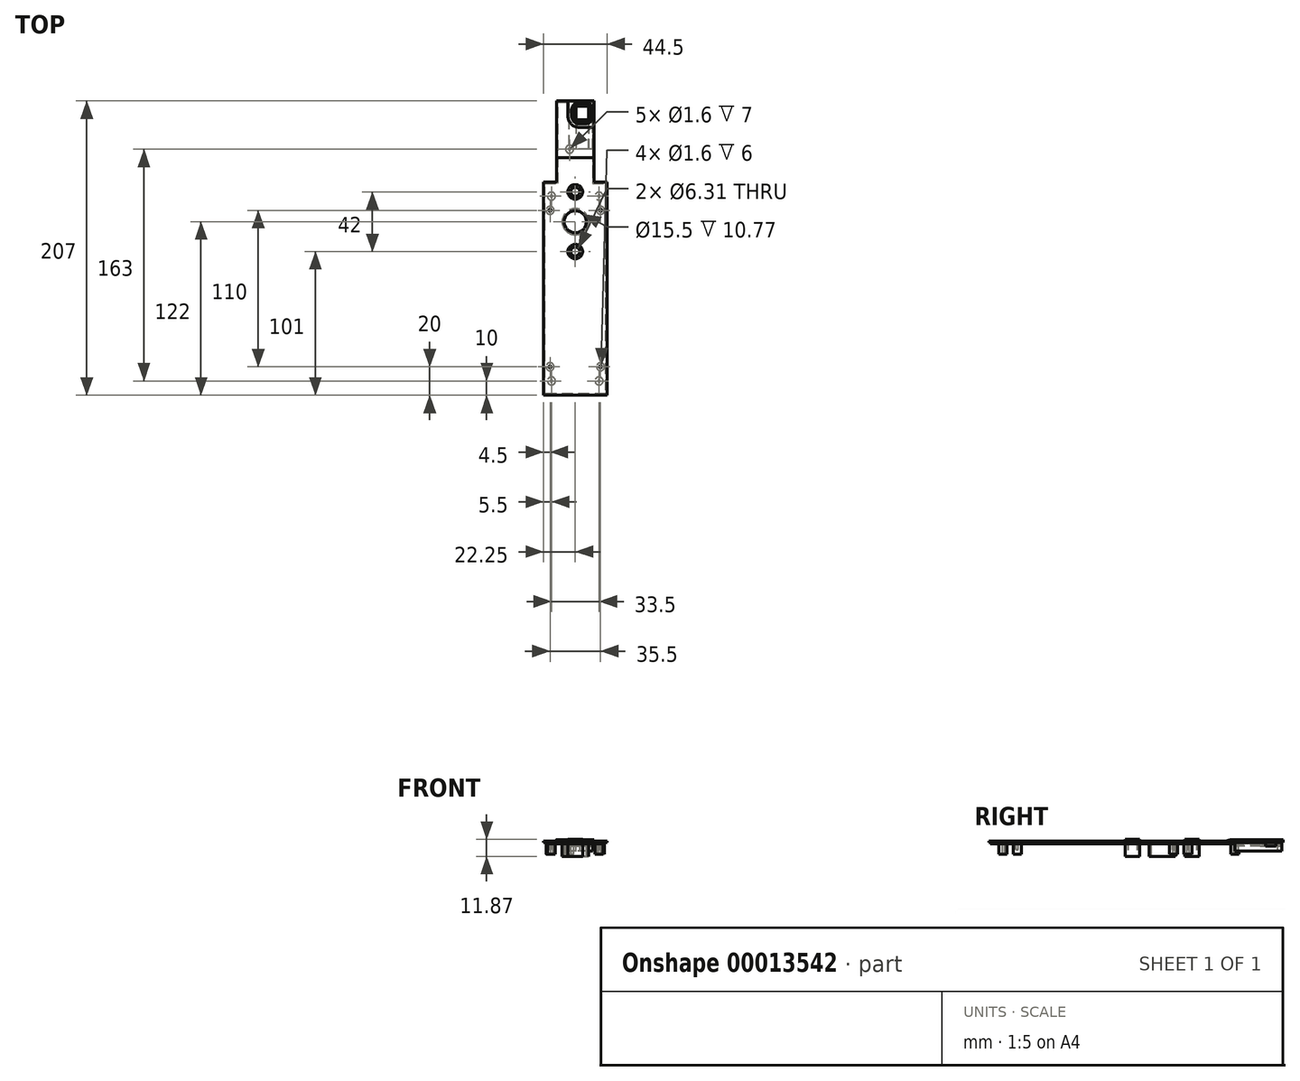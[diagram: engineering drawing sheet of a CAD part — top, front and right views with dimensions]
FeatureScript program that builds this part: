
annotation { "Feature Type Name" : "Feature", "Feature Type Description" : "" }
export const myFeature = defineFeature(function(context is Context, id is Id, definition is map)
    precondition{}
    {
        {
            var Q0;
            Q0=qCreatedBy(makeId("Top.planeOp"),FACE);
            var sketch = newSketch(context, id + "F0", { "sketchPlane" : qUnion([Q0])});
            skLineSegment(sketch, "E0.bottom", {"start": v(0, 0) * mm, "end": v(43.5, 0) * mm});
            skLineSegment(sketch, "E0.right", {"start": v(43.5, 0) * mm, "end": v(43.5, 150) * mm});
            skLineSegment(sketch, "E0.left", {"start": v(0, 0) * mm, "end": v(0, 150) * mm});
            skLineSegment(sketch, "E1", {"start": v(35.5, 207) * mm, "end": v(9, 207) * mm, "construction": true});
            skLineSegment(sketch, "E2", {"start": v(35.5, 150) * mm, "end": v(35.5, 207) * mm, "construction": true});
            skLineSegment(sketch, "E3", {"start": v(43.5, 150) * mm, "end": v(35.5, 150) * mm});
            skLineSegment(sketch, "E4", {"start": v(9, 207) * mm, "end": v(9, 150) * mm, "construction": true});
            skLineSegment(sketch, "E5", {"start": v(9, 150) * mm, "end": v(0, 150) * mm});
            skLineSegment(sketch, "E6", {"start": v(9, 150) * mm, "end": v(9, 64) * mm});
            skLineSegment(sketch, "E7", {"start": v(9, 64) * mm, "end": v(35.5, 64) * mm});
            skLineSegment(sketch, "E8", {"start": v(35.5, 64) * mm, "end": v(35.5, 150) * mm});
            skSolve(sketch);
        }
        {
            var Q0;
            Q0 = qSketchRegion(id + "F0", true);
            extrude(context, id + "F1", {"entities" : qUnion([Q0]), "depth" : 2 * mm});
        }
        {
            var Q0;
            Q0=makeQuery(id+"F1.opExtrude","CAP_FACE",FACE,{"disambiguationData":[OSD([sQuery(id+"F0.wireOp",EDGE,"E0.bottom"),sQuery(id+"F0.wireOp",EDGE,"E0.right"),sQuery(id+"F0.wireOp",EDGE,"E0.left"),sQuery(id+"F0.wireOp",EDGE,"E3"),sQuery(id+"F0.wireOp",EDGE,"E5"),sQuery(id+"F0.wireOp",EDGE,"E6"),sQuery(id+"F0.wireOp",EDGE,"E7"),sQuery(id+"F0.wireOp",EDGE,"E8")])],"isStart":true});
            var sketch = newSketch(context, id + "F2", { "sketchPlane" : qUnion([Q0])});
            skLineSegment(sketch, "E9", {"start": v(35.5, -64) * mm, "end": v(9, -64) * mm});
            skLineSegment(sketch, "E10", {"start": v(9, -64) * mm, "end": v(9, -150) * mm});
            skLineSegment(sketch, "E11", {"start": v(9, -150) * mm, "end": v(9, -113) * mm});
            skLineSegment(sketch, "E12", {"start": v(35.5, -64) * mm, "end": v(35.5, -143) * mm});
            skLineSegment(sketch, "E13", {"start": v(35.5, -143) * mm, "end": v(35.5, -150.46) * mm});
            skLineSegment(sketch, "E14", {"start": v(35.5, -150.46) * mm, "end": v(35.5, -207) * mm});
            skLineSegment(sketch, "E15", {"start": v(35.5, -207) * mm, "end": v(9, -207) * mm});
            skLineSegment(sketch, "E16", {"start": v(9, -207) * mm, "end": v(9, -113) * mm});
            skLineSegment(sketch, "E17", {"start": v(22.25, -64) * mm, "end": v(22.25, -237) * mm, "construction": true});
            skPoint(sketch, "E18", {"position": v(22.25, -237) * mm});
            skSolve(sketch);
        }
        {
            var Q0;
            Q0 = qSketchRegion(id + "F2", true);
            extrude(context, id + "F3", {"entities" : qUnion([Q0]), "operationType" : NewBodyOperationType.ADD, "oppositeDirection" : true, "depth" : 2 * mm});
        }
        {
            var Q0;
            Q0=makeQuery(id+"F1.opExtrude","CAP_FACE",FACE,{"disambiguationData":[OSD([sQuery(id+"F0.wireOp",EDGE,"E0.bottom"),sQuery(id+"F0.wireOp",EDGE,"E0.right"),sQuery(id+"F0.wireOp",EDGE,"E0.left"),sQuery(id+"F0.wireOp",EDGE,"E3"),sQuery(id+"F0.wireOp",EDGE,"E5"),sQuery(id+"F0.wireOp",EDGE,"E6"),sQuery(id+"F0.wireOp",EDGE,"E7"),sQuery(id+"F0.wireOp",EDGE,"E8")])],"isStart":true});
            var sketch = newSketch(context, id + "F4", { "sketchPlane" : qUnion([Q0])});
            skLineSegment(sketch, "E19", {"start": v(43.5, -150) * mm, "end": v(43.5, 0) * mm});
            skLineSegment(sketch, "E20", {"start": v(44.5, 0) * mm, "end": v(43.5, 0) * mm});
            skLineSegment(sketch, "E21", {"start": v(44.5, 0) * mm, "end": v(44.5, -150) * mm});
            skLineSegment(sketch, "E22", {"start": v(43.5, -150) * mm, "end": v(44.5, -150) * mm});
            skSolve(sketch);
        }
        {
            var Q0;
            Q0 = qSketchRegion(id + "F4", true);
            extrude(context, id + "F5", {"entities" : qUnion([Q0]), "operationType" : NewBodyOperationType.ADD, "oppositeDirection" : true, "depth" : 2 * mm});
        }
        {
            var Q0;
            Q0=makeQuery(id+"F3.opExtrude","CAP_FACE",FACE,{"disambiguationData":[OSD([sQuery(id+"F2.wireOp",EDGE,"E9"),sQuery(id+"F2.wireOp",EDGE,"E10"),sQuery(id+"F2.wireOp",EDGE,"E11"),sQuery(id+"F2.wireOp",EDGE,"E12"),sQuery(id+"F2.wireOp",EDGE,"E13"),sQuery(id+"F2.wireOp",EDGE,"E14"),sQuery(id+"F2.wireOp",EDGE,"E15"),sQuery(id+"F2.wireOp",EDGE,"E16")])],"isStart":true});
            var sketch = newSketch(context, id + "F6", { "sketchPlane" : qUnion([Q0])});
            skLineSegment(sketch, "E23", {"start": v(1, -149) * mm, "end": v(10, -149) * mm});
            skLineSegment(sketch, "E24", {"start": v(10, -149) * mm, "end": v(10, -206) * mm});
            skLineSegment(sketch, "E25", {"start": v(10, -206) * mm, "end": v(34.5, -206) * mm});
            skLineSegment(sketch, "E26", {"start": v(34.5, -206) * mm, "end": v(34.5, -149) * mm});
            skLineSegment(sketch, "E27", {"start": v(34.5, -149) * mm, "end": v(43.5, -149) * mm});
            skLineSegment(sketch, "E28", {"start": v(43.5, -149) * mm, "end": v(43.5, -1) * mm});
            skLineSegment(sketch, "E29", {"start": v(43.5, -1) * mm, "end": v(1, -1) * mm});
            skLineSegment(sketch, "E30", {"start": v(1, -1) * mm, "end": v(1, -149) * mm});
            skLineSegment(sketch, "E31", {"start": v(9, -207) * mm, "end": v(35.5, -207) * mm});
            skLineSegment(sketch, "E32", {"start": v(44.5, -150) * mm, "end": v(44.5, 0) * mm});
            skLineSegment(sketch, "E33", {"start": v(44.5, 0) * mm, "end": v(0, 0) * mm});
            skLineSegment(sketch, "E34", {"start": v(0, 0) * mm, "end": v(0, -150) * mm});
            skLineSegment(sketch, "E35", {"start": v(44.5, -150) * mm, "end": v(35.5, -150) * mm});
            skLineSegment(sketch, "E36", {"start": v(35.5, -150) * mm, "end": v(35.5, -207) * mm});
            skLineSegment(sketch, "E37", {"start": v(35.5, -207) * mm, "end": v(35.5, -207) * mm});
            skLineSegment(sketch, "E38", {"start": v(0, -150) * mm, "end": v(9, -150) * mm});
            skLineSegment(sketch, "E39", {"start": v(9, -150) * mm, "end": v(9, -207) * mm});
            skLineSegment(sketch, "E40", {"start": v(9, -207) * mm, "end": v(9, -207) * mm});
            skSolve(sketch);
        }
        {
            var Q0;
            Q0 = qSketchRegion(id + "F6", true);
            extrude(context, id + "F7", {"entities" : qUnion([Q0]), "operationType" : NewBodyOperationType.REMOVE, "oppositeDirection" : true, "depth" : 1 * mm});
        }
        {
            var Q0;
            Q0=makeQuery(id+"F5.boolean.opBoolean","MERGE",FACE,{"derivedFrom":[makeQuery(id+"F3.boolean.opBoolean","MERGE",FACE,{"derivedFrom":[makeQuery(id+"F1.opExtrude","CAP_FACE",FACE,{"disambiguationData":[OSD([sQuery(id+"F0.wireOp",EDGE,"E0.bottom"),sQuery(id+"F0.wireOp",EDGE,"E0.right"),sQuery(id+"F0.wireOp",EDGE,"E0.left"),sQuery(id+"F0.wireOp",EDGE,"E3"),sQuery(id+"F0.wireOp",EDGE,"E5"),sQuery(id+"F0.wireOp",EDGE,"E6"),sQuery(id+"F0.wireOp",EDGE,"E7"),sQuery(id+"F0.wireOp",EDGE,"E8")])],"isStart":false}),makeQuery(id+"F3.opExtrude","CAP_FACE",FACE,{"disambiguationData":[OSD([sQuery(id+"F2.wireOp",EDGE,"E9"),sQuery(id+"F2.wireOp",EDGE,"E10"),sQuery(id+"F2.wireOp",EDGE,"E11"),sQuery(id+"F2.wireOp",EDGE,"E12"),sQuery(id+"F2.wireOp",EDGE,"E13"),sQuery(id+"F2.wireOp",EDGE,"E14"),sQuery(id+"F2.wireOp",EDGE,"E15"),sQuery(id+"F2.wireOp",EDGE,"E16")])],"isStart":false})]}),makeQuery(id+"F5.opExtrude","CAP_FACE",FACE,{"disambiguationData":[OSD([sQuery(id+"F4.wireOp",EDGE,"E19"),sQuery(id+"F4.wireOp",EDGE,"E20"),sQuery(id+"F4.wireOp",EDGE,"E21"),sQuery(id+"F4.wireOp",EDGE,"E22")])],"isStart":false})]});
            var sketch = newSketch(context, id + "F8", { "sketchPlane" : qUnion([Q0])});
            skCircle(sketch, "E41", {"center": v(22.25, 122) * mm, "radius": 7.75 * mm});
            skLineSegment(sketch, "E42", {"start": v(22.25, 207) * mm, "end": v(22.25, 78.47) * mm, "construction": true});
            skSolve(sketch);
        }
        {
            var Q0;
            Q0 = qSketchRegion(id + "F8", true);
            var Q1;
            Q1=makeQuery(id+"F5.boolean.opBoolean","MERGE",FACE,{"derivedFrom":[makeQuery(id+"F3.boolean.opBoolean","MERGE",FACE,{"derivedFrom":[makeQuery(id+"F1.opExtrude","CAP_FACE",FACE,{"disambiguationData":[OSD([sQuery(id+"F0.wireOp",EDGE,"E0.bottom"),sQuery(id+"F0.wireOp",EDGE,"E0.right"),sQuery(id+"F0.wireOp",EDGE,"E0.left"),sQuery(id+"F0.wireOp",EDGE,"E3"),sQuery(id+"F0.wireOp",EDGE,"E5"),sQuery(id+"F0.wireOp",EDGE,"E6"),sQuery(id+"F0.wireOp",EDGE,"E7"),sQuery(id+"F0.wireOp",EDGE,"E8")])],"isStart":true}),makeQuery(id+"F3.opExtrude","CAP_FACE",FACE,{"disambiguationData":[OSD([sQuery(id+"F2.wireOp",EDGE,"E9"),sQuery(id+"F2.wireOp",EDGE,"E10"),sQuery(id+"F2.wireOp",EDGE,"E11"),sQuery(id+"F2.wireOp",EDGE,"E12"),sQuery(id+"F2.wireOp",EDGE,"E13"),sQuery(id+"F2.wireOp",EDGE,"E14"),sQuery(id+"F2.wireOp",EDGE,"E15"),sQuery(id+"F2.wireOp",EDGE,"E16")])],"isStart":true})]}),makeQuery(id+"F5.opExtrude","CAP_FACE",FACE,{"disambiguationData":[OSD([sQuery(id+"F4.wireOp",EDGE,"E19"),sQuery(id+"F4.wireOp",EDGE,"E20"),sQuery(id+"F4.wireOp",EDGE,"E21"),sQuery(id+"F4.wireOp",EDGE,"E22")])],"isStart":true})]});
            extrude(context, id + "F9", {"entities" : qUnion([Q0]), "operationType" : NewBodyOperationType.REMOVE, "endBound" : BoundingType.UP_TO_SURFACE, "oppositeDirection" : true, "endBoundEntityFace" : qUnion([Q1]), "depth" : 25 * mm});
        }
        {
            var Q0;
            Q0=makeQuery(id+"F5.boolean.opBoolean","MERGE",FACE,{"derivedFrom":[makeQuery(id+"F3.boolean.opBoolean","MERGE",FACE,{"derivedFrom":[makeQuery(id+"F1.opExtrude","CAP_FACE",FACE,{"disambiguationData":[OSD([sQuery(id+"F0.wireOp",EDGE,"E0.bottom"),sQuery(id+"F0.wireOp",EDGE,"E0.right"),sQuery(id+"F0.wireOp",EDGE,"E0.left"),sQuery(id+"F0.wireOp",EDGE,"E3"),sQuery(id+"F0.wireOp",EDGE,"E5"),sQuery(id+"F0.wireOp",EDGE,"E6"),sQuery(id+"F0.wireOp",EDGE,"E7"),sQuery(id+"F0.wireOp",EDGE,"E8")])],"isStart":false}),makeQuery(id+"F3.opExtrude","CAP_FACE",FACE,{"disambiguationData":[OSD([sQuery(id+"F2.wireOp",EDGE,"E9"),sQuery(id+"F2.wireOp",EDGE,"E10"),sQuery(id+"F2.wireOp",EDGE,"E11"),sQuery(id+"F2.wireOp",EDGE,"E12"),sQuery(id+"F2.wireOp",EDGE,"E13"),sQuery(id+"F2.wireOp",EDGE,"E14"),sQuery(id+"F2.wireOp",EDGE,"E15"),sQuery(id+"F2.wireOp",EDGE,"E16")])],"isStart":false})]}),makeQuery(id+"F5.opExtrude","CAP_FACE",FACE,{"disambiguationData":[OSD([sQuery(id+"F4.wireOp",EDGE,"E19"),sQuery(id+"F4.wireOp",EDGE,"E20"),sQuery(id+"F4.wireOp",EDGE,"E21"),sQuery(id+"F4.wireOp",EDGE,"E22")])],"isStart":false})]});
            var sketch = newSketch(context, id + "F10", { "sketchPlane" : qUnion([Q0])});
            skLineSegment(sketch, "E43.bottom", {"start": v(31.7, 203.2) * mm, "end": v(22.7, 203.2) * mm});
            skLineSegment(sketch, "E43.right", {"start": v(22.7, 203.2) * mm, "end": v(22.7, 193.7) * mm});
            skLineSegment(sketch, "E43.top", {"start": v(22.7, 193.7) * mm, "end": v(31.7, 193.7) * mm});
            skLineSegment(sketch, "E43.left", {"start": v(31.7, 203.2) * mm, "end": v(31.7, 193.7) * mm});
            skLineSegment(sketch, "E44", {"start": v(33.5, 176.54) * mm, "end": v(33.5, 205) * mm, "construction": true});
            skLineSegment(sketch, "E45", {"start": v(33.5, 205) * mm, "end": v(10.5, 205) * mm, "construction": true});
            skLineSegment(sketch, "E46", {"start": v(10.5, 205) * mm, "end": v(10.5, 175.62) * mm, "construction": true});
            skSolve(sketch);
        }
        {
            var Q0;
            Q0 = qSketchRegion(id + "F10", true);
            var Q1;
            Q1=makeQuery(id+"F5.boolean.opBoolean","MERGE",FACE,{"derivedFrom":[makeQuery(id+"F3.boolean.opBoolean","MERGE",FACE,{"derivedFrom":[makeQuery(id+"F1.opExtrude","CAP_FACE",FACE,{"disambiguationData":[OSD([sQuery(id+"F0.wireOp",EDGE,"E0.bottom"),sQuery(id+"F0.wireOp",EDGE,"E0.right"),sQuery(id+"F0.wireOp",EDGE,"E0.left"),sQuery(id+"F0.wireOp",EDGE,"E3"),sQuery(id+"F0.wireOp",EDGE,"E5"),sQuery(id+"F0.wireOp",EDGE,"E6"),sQuery(id+"F0.wireOp",EDGE,"E7"),sQuery(id+"F0.wireOp",EDGE,"E8")])],"isStart":true}),makeQuery(id+"F3.opExtrude","CAP_FACE",FACE,{"disambiguationData":[OSD([sQuery(id+"F2.wireOp",EDGE,"E9"),sQuery(id+"F2.wireOp",EDGE,"E10"),sQuery(id+"F2.wireOp",EDGE,"E12"),sQuery(id+"F2.wireOp",EDGE,"E13"),sQuery(id+"F2.wireOp",EDGE,"E14"),sQuery(id+"F2.wireOp",EDGE,"E15"),sQuery(id+"F2.wireOp",EDGE,"E16")])],"isStart":true})]}),makeQuery(id+"F5.opExtrude","CAP_FACE",FACE,{"disambiguationData":[OSD([sQuery(id+"F4.wireOp",EDGE,"E19"),sQuery(id+"F4.wireOp",EDGE,"E20"),sQuery(id+"F4.wireOp",EDGE,"E21"),sQuery(id+"F4.wireOp",EDGE,"E22")])],"isStart":true})]});
            extrude(context, id + "F11", {"entities" : qUnion([Q0]), "operationType" : NewBodyOperationType.REMOVE, "endBound" : BoundingType.UP_TO_SURFACE, "oppositeDirection" : true, "endBoundEntityFace" : qUnion([Q1]), "depth" : 25 * mm});
        }
        {
            var Q0;
            {var subQ2=sQuery(id+"F4.wireOp",EDGE,"E21");Q0=makeQuery(id+"F4.imprint","IMPRINT",FACE,{"disambiguationData":[TD([[makeQuery(id+"F4.imprint","IMPRINT",EDGE,{"derivedFrom":subQ2}),-1.0]])]});}
            var sketch = newSketch(context, id + "F12", { "sketchPlane" : qUnion([Q0])});
            skPoint(sketch, "E47.8.MirrorP", {"position": v(5.5, -10) * mm});
            skPoint(sketch, "E47.9.MirrorP", {"position": v(18.25, -173) * mm});
            skPoint(sketch, "E47.16.MirrorP", {"position": v(39, -10) * mm});
            skPoint(sketch, "E48.16.MirrorP", {"position": v(39, -140) * mm});
            skPoint(sketch, "E49.16.MirrorP", {"position": v(5.5, -140) * mm});
            skLineSegment(sketch, "E50", {"start": v(22.25, -207) * mm, "end": v(22.25, 0) * mm, "construction": true});
            skCircle(sketch, "E51", {"center": v(39, -140) * mm, "radius": 2.8 * mm});
            skCircle(sketch, "E52", {"center": v(5.5, -140) * mm, "radius": 2.8 * mm});
            skCircle(sketch, "E53", {"center": v(39, -10) * mm, "radius": 2.8 * mm});
            skCircle(sketch, "E54", {"center": v(5.5, -10) * mm, "radius": 2.8 * mm});
            skCircle(sketch, "E55", {"center": v(18.25, -173) * mm, "radius": 2.8 * mm});
            skLineSegment(sketch, "E56", {"start": v(5.5, -149) * mm, "end": v(5.5, 0) * mm, "construction": true});
            skLineSegment(sketch, "E57", {"start": v(39, -149) * mm, "end": v(39, 0) * mm, "construction": true});
            skSolve(sketch);
        }
        {
            var Q0;
            Q0 = qSketchRegion(id + "F12", true);
            extrude(context, id + "F13", {"entities" : qUnion([Q0]), "operationType" : NewBodyOperationType.ADD, "depth" : 7.1 * mm});
        }
        {
            var Q0;
            Q0=makeQuery(id+"F13.opExtrude","CAP_FACE",FACE,{"disambiguationData":[OSD([sQuery(id+"F12.wireOp",EDGE,"E55")])],"isStart":false});
            var sketch = newSketch(context, id + "F14", { "sketchPlane" : qUnion([Q0])});
            skCircle(sketch, "E58", {"center": v(18.25, -173) * mm, "radius": 0.8 * mm});
            skCircle(sketch, "E59", {"center": v(5.5, -140) * mm, "radius": 0.8 * mm});
            skCircle(sketch, "E60", {"center": v(39, -140) * mm, "radius": 0.8 * mm});
            skCircle(sketch, "E61", {"center": v(39, -10) * mm, "radius": 0.8 * mm});
            skCircle(sketch, "E62", {"center": v(5.5, -10) * mm, "radius": 0.8 * mm});
            skSolve(sketch);
        }
        {
            var Q0;
            Q0 = qSketchRegion(id + "F14", true);
            extrude(context, id + "F15", {"entities" : qUnion([Q0]), "operationType" : NewBodyOperationType.REMOVE, "oppositeDirection" : true, "depth" : 7 * mm});
        }
        {
            var Q0;
            Q0=makeQuery(id+"F4.imprint","IMPRINT",FACE,{"disambiguationData":[TD([[makeQuery(id+"F4.imprint","IMPRINT",EDGE,{"derivedFrom":sQuery(id+"F4.wireOp",EDGE,"E19")}),1.0]])]});
            var sketch = newSketch(context, id + "F16", { "sketchPlane" : qUnion([Q0])});
            skCircle(sketch, "E63", {"center": v(40, -20) * mm, "radius": 2.8 * mm});
            skCircle(sketch, "E64", {"center": v(4.5, -130) * mm, "radius": 2.8 * mm});
            skLineSegment(sketch, "E65", {"start": v(40, -150) * mm, "end": v(40, 0) * mm, "construction": true});
            skLineSegment(sketch, "E66", {"start": v(4.5, -140) * mm, "end": v(4.5, -10) * mm, "construction": true});
            skCircle(sketch, "E67", {"center": v(4.5, -20) * mm, "radius": 2.8 * mm});
            skCircle(sketch, "E68", {"center": v(40, -130) * mm, "radius": 2.8 * mm});
            skLineSegment(sketch, "E69", {"start": v(5.5, -10) * mm, "end": v(0, -10) * mm, "construction": true});
            skLineSegment(sketch, "E70", {"start": v(5.5, -140) * mm, "end": v(1.03, -140) * mm, "construction": true});
            skSolve(sketch);
        }
        {
            var Q0;
            Q0 = qSketchRegion(id + "F16", true);
            var Q1;
            Q1=makeQuery(id+"F13.opExtrude","CAP_FACE",FACE,{"disambiguationData":[OSD([sQuery(id+"F12.wireOp",EDGE,"E53")])],"isStart":false});
            extrude(context, id + "F17", {"entities" : qUnion([Q0]), "operationType" : NewBodyOperationType.ADD, "endBound" : BoundingType.UP_TO_SURFACE, "endBoundEntityFace" : qUnion([Q1]), "depth" : 25 * mm});
        }
        {
            var Q0;
            Q0=makeQuery(id+"F5.boolean.opBoolean","MERGE",FACE,{"derivedFrom":[makeQuery(id+"F3.boolean.opBoolean","MERGE",FACE,{"derivedFrom":[makeQuery(id+"F1.opExtrude","CAP_FACE",FACE,{"disambiguationData":[OSD([sQuery(id+"F0.wireOp",EDGE,"E0.bottom"),sQuery(id+"F0.wireOp",EDGE,"E0.right"),sQuery(id+"F0.wireOp",EDGE,"E0.left"),sQuery(id+"F0.wireOp",EDGE,"E3"),sQuery(id+"F0.wireOp",EDGE,"E5"),sQuery(id+"F0.wireOp",EDGE,"E6"),sQuery(id+"F0.wireOp",EDGE,"E7"),sQuery(id+"F0.wireOp",EDGE,"E8")])],"isStart":false}),makeQuery(id+"F3.opExtrude","CAP_FACE",FACE,{"disambiguationData":[OSD([sQuery(id+"F2.wireOp",EDGE,"E9"),sQuery(id+"F2.wireOp",EDGE,"E10"),sQuery(id+"F2.wireOp",EDGE,"E12"),sQuery(id+"F2.wireOp",EDGE,"E14"),sQuery(id+"F2.wireOp",EDGE,"E15"),sQuery(id+"F2.wireOp",EDGE,"E16")])],"isStart":false})]}),makeQuery(id+"F5.opExtrude","CAP_FACE",FACE,{"disambiguationData":[OSD([sQuery(id+"F4.wireOp",EDGE,"E19"),sQuery(id+"F4.wireOp",EDGE,"E20"),sQuery(id+"F4.wireOp",EDGE,"E21"),sQuery(id+"F4.wireOp",EDGE,"E22")])],"isStart":false})]});
            var sketch = newSketch(context, id + "F18", { "sketchPlane" : qUnion([Q0])});
            skCircle(sketch, "E71", {"center": v(4.5, 130) * mm, "radius": 0.8 * mm});
            skCircle(sketch, "E72", {"center": v(40, 130) * mm, "radius": 0.8 * mm});
            skCircle(sketch, "E73", {"center": v(4.5, 20) * mm, "radius": 0.8 * mm});
            skCircle(sketch, "E74", {"center": v(40, 20) * mm, "radius": 0.8 * mm});
            skSolve(sketch);
        }
        {
            var Q0;
            Q0 = qSketchRegion(id + "F18", true);
            extrude(context, id + "F19", {"entities" : qUnion([Q0]), "operationType" : NewBodyOperationType.REMOVE, "oppositeDirection" : true, "depth" : 6 * mm});
        }
        {
            var Q0;
            Q0=makeQuery(id+"F4.imprint","IMPRINT",FACE,{"disambiguationData":[TD([[makeQuery(id+"F4.imprint","IMPRINT",EDGE,{"derivedFrom":sQuery(id+"F4.wireOp",EDGE,"E19")}),-1.0]])]});
            var sketch = newSketch(context, id + "F20", { "sketchPlane" : qUnion([Q0])});
            skLineSegment(sketch, "E75", {"start": v(34.5, -206) * mm, "end": v(17.7, -206) * mm});
            skLineSegment(sketch, "E76", {"start": v(17.7, -206) * mm, "end": v(17.7, -173) * mm});
            skLineSegment(sketch, "E77", {"start": v(34.5, -173) * mm, "end": v(34.5, -206) * mm});
            skLineSegment(sketch, "E78", {"start": v(31.7, -198.44) * mm, "end": v(34.5, -198.44) * mm, "construction": true});
            skLineSegment(sketch, "E79", {"start": v(31.7, -203.2) * mm, "end": v(22.7, -203.2) * mm});
            skLineSegment(sketch, "E80", {"start": v(22.7, -203.2) * mm, "end": v(22.7, -173) * mm});
            skLineSegment(sketch, "E81", {"start": v(31.7, -173) * mm, "end": v(31.7, -203.2) * mm});
            skLineSegment(sketch, "E82", {"start": v(34.5, -173) * mm, "end": v(31.7, -173) * mm});
            skLineSegment(sketch, "E83", {"start": v(22.7, -173) * mm, "end": v(17.7, -173) * mm});
            skSolve(sketch);
        }
        {
            var Q0;
            Q0 = qSketchRegion(id + "F20", true);
            extrude(context, id + "F21", {"entities" : qUnion([Q0]), "operationType" : NewBodyOperationType.ADD, "depth" : 5 * mm});
        }
        {
            var Q0;
            Q0=makeQuery(id+"F4.imprint","IMPRINT",FACE,{"disambiguationData":[TD([[makeQuery(id+"F4.imprint","IMPRINT",EDGE,{"derivedFrom":sQuery(id+"F4.wireOp",EDGE,"E19")}),-1.0]])]});
            var sketch = newSketch(context, id + "F22", { "sketchPlane" : qUnion([Q0])});
            skLineSegment(sketch, "E84.bottom", {"start": v(31.7, -193.7) * mm, "end": v(22.7, -193.7) * mm});
            skLineSegment(sketch, "E84.top", {"start": v(31.7, -173) * mm, "end": v(22.7, -173) * mm});
            skLineSegment(sketch, "E84.left", {"start": v(31.7, -193.7) * mm, "end": v(31.7, -173) * mm});
            skLineSegment(sketch, "E84.right", {"start": v(22.7, -193.7) * mm, "end": v(22.7, -173) * mm});
            skSolve(sketch);
        }
        {
            var Q0;
            Q0 = qSketchRegion(id + "F22", true);
            extrude(context, id + "F23", {"entities" : qUnion([Q0]), "operationType" : NewBodyOperationType.ADD, "depth" : 1.48 * mm});
        }
        {
            var Q0;
            Q0=makeQuery(id+"F4.imprint","IMPRINT",FACE,{"disambiguationData":[TD([[makeQuery(id+"F4.imprint","IMPRINT",EDGE,{"derivedFrom":sQuery(id+"F4.wireOp",EDGE,"E19")}),-1.0]])]});
            var sketch = newSketch(context, id + "F24", { "sketchPlane" : qUnion([Q0])});
            skLineSegment(sketch, "E85", {"start": v(22.25, -122) * mm, "end": v(22.25, 0) * mm, "construction": true});
            skLineSegment(sketch, "E86", {"start": v(22.25, -122) * mm, "end": v(22.25, -206) * mm, "construction": true});
            skCircle(sketch, "E87", {"center": v(22.25, -143) * mm, "radius": 5.16 * mm});
            skCircle(sketch, "E88", {"center": v(22.25, -101) * mm, "radius": 5.16 * mm});
            skLineSegment(sketch, "E89", {"start": v(22.25, -143) * mm, "end": v(22.25, -122) * mm, "construction": true});
            skLineSegment(sketch, "E90", {"start": v(22.25, -122) * mm, "end": v(22.25, -101) * mm, "construction": true});
            skSolve(sketch);
        }
        {
            var Q0;
            Q0 = qSketchRegion(id + "F24", true);
            var Q1;
            Q1=makeQuery(id+"F5.boolean.opBoolean","MERGE",FACE,{"derivedFrom":[makeQuery(id+"F3.boolean.opBoolean","MERGE",FACE,{"derivedFrom":[makeQuery(id+"F1.opExtrude","CAP_FACE",FACE,{"disambiguationData":[OSD([sQuery(id+"F0.wireOp",EDGE,"E0.bottom"),sQuery(id+"F0.wireOp",EDGE,"E0.right"),sQuery(id+"F0.wireOp",EDGE,"E0.left"),sQuery(id+"F0.wireOp",EDGE,"E3"),sQuery(id+"F0.wireOp",EDGE,"E5"),sQuery(id+"F0.wireOp",EDGE,"E6"),sQuery(id+"F0.wireOp",EDGE,"E7"),sQuery(id+"F0.wireOp",EDGE,"E8")])],"isStart":false}),makeQuery(id+"F3.opExtrude","CAP_FACE",FACE,{"disambiguationData":[OSD([sQuery(id+"F2.wireOp",EDGE,"E9"),sQuery(id+"F2.wireOp",EDGE,"E10"),sQuery(id+"F2.wireOp",EDGE,"E12"),sQuery(id+"F2.wireOp",EDGE,"E13"),sQuery(id+"F2.wireOp",EDGE,"E14"),sQuery(id+"F2.wireOp",EDGE,"E15"),sQuery(id+"F2.wireOp",EDGE,"E16")])],"isStart":false})]}),makeQuery(id+"F5.opExtrude","CAP_FACE",FACE,{"disambiguationData":[OSD([sQuery(id+"F4.wireOp",EDGE,"E19"),sQuery(id+"F4.wireOp",EDGE,"E20"),sQuery(id+"F4.wireOp",EDGE,"E21"),sQuery(id+"F4.wireOp",EDGE,"E22")])],"isStart":false})]});
            extrude(context, id + "F25", {"entities" : qUnion([Q0]), "operationType" : NewBodyOperationType.ADD, "endBoundEntityFace" : qUnion([Q1]), "depth" : 8.77 * mm});
        }
        {
            var Q0;
            Q0=makeQuery(id+"F25.opExtrude","CAP_FACE",FACE,{"disambiguationData":[OSD([sQuery(id+"F24.wireOp",EDGE,"E87")])],"isStart":false});
            var sketch = newSketch(context, id + "F26", { "sketchPlane" : qUnion([Q0])});
            skCircle(sketch, "E91", {"center": v(22.25, -143) * mm, "radius": 3.16 * mm});
            skCircle(sketch, "E92", {"center": v(22.25, -101) * mm, "radius": 3.16 * mm});
            skSolve(sketch);
        }
        {
            var Q0;
            Q0 = qSketchRegion(id + "F26", true);
            var Q1;
            Q1=makeQuery(id+"F5.boolean.opBoolean","MERGE",FACE,{"derivedFrom":[makeQuery(id+"F3.boolean.opBoolean","MERGE",FACE,{"derivedFrom":[makeQuery(id+"F1.opExtrude","CAP_FACE",FACE,{"disambiguationData":[OSD([sQuery(id+"F0.wireOp",EDGE,"E0.bottom"),sQuery(id+"F0.wireOp",EDGE,"E0.right"),sQuery(id+"F0.wireOp",EDGE,"E0.left"),sQuery(id+"F0.wireOp",EDGE,"E3"),sQuery(id+"F0.wireOp",EDGE,"E5"),sQuery(id+"F0.wireOp",EDGE,"E6"),sQuery(id+"F0.wireOp",EDGE,"E7"),sQuery(id+"F0.wireOp",EDGE,"E8")])],"isStart":false}),makeQuery(id+"F3.opExtrude","CAP_FACE",FACE,{"disambiguationData":[OSD([sQuery(id+"F2.wireOp",EDGE,"E9"),sQuery(id+"F2.wireOp",EDGE,"E10"),sQuery(id+"F2.wireOp",EDGE,"E12"),sQuery(id+"F2.wireOp",EDGE,"E13"),sQuery(id+"F2.wireOp",EDGE,"E14"),sQuery(id+"F2.wireOp",EDGE,"E15"),sQuery(id+"F2.wireOp",EDGE,"E16")])],"isStart":false})]}),makeQuery(id+"F5.opExtrude","CAP_FACE",FACE,{"disambiguationData":[OSD([sQuery(id+"F4.wireOp",EDGE,"E19"),sQuery(id+"F4.wireOp",EDGE,"E20"),sQuery(id+"F4.wireOp",EDGE,"E21"),sQuery(id+"F4.wireOp",EDGE,"E22")])],"isStart":false})]});
            extrude(context, id + "F27", {"entities" : qUnion([Q0]), "operationType" : NewBodyOperationType.REMOVE, "endBound" : BoundingType.UP_TO_SURFACE, "oppositeDirection" : true, "endBoundEntityFace" : qUnion([Q1]), "depth" : 25 * mm});
        }
        {
            var Q0;
            Q0=makeQuery(id+"F4.imprint","IMPRINT",FACE,{"disambiguationData":[TD([[makeQuery(id+"F4.imprint","IMPRINT",EDGE,{"derivedFrom":sQuery(id+"F4.wireOp",EDGE,"E19")}),-1.0]])]});
            var sketch = newSketch(context, id + "F28", { "sketchPlane" : qUnion([Q0])});
            skCircle(sketch, "E93", {"center": v(22.25, -122) * mm, "radius": 9.25 * mm});
            skCircle(sketch, "E94", {"center": v(22.25, -122) * mm, "radius": 7.75 * mm});
            skSolve(sketch);
        }
        {
            var Q0;
            Q0 = qSketchRegion(id + "F28", true);
            var Q1;
            Q1=makeQuery(id+"F25.opExtrude","CAP_FACE",FACE,{"disambiguationData":[OSD([sQuery(id+"F24.wireOp",EDGE,"E87")])],"isStart":false});
            extrude(context, id + "F29", {"entities" : qUnion([Q0]), "operationType" : NewBodyOperationType.ADD, "endBound" : BoundingType.UP_TO_SURFACE, "endBoundEntityFace" : qUnion([Q1]), "depth" : 25 * mm});
        }
        {
            var Q0;
            Q0=makeQuery(id+"F5.boolean.opBoolean","MERGE",FACE,{"derivedFrom":[makeQuery(id+"F3.boolean.opBoolean","MERGE",FACE,{"derivedFrom":[makeQuery(id+"F1.opExtrude","CAP_FACE",FACE,{"disambiguationData":[OSD([sQuery(id+"F0.wireOp",EDGE,"E0.bottom"),sQuery(id+"F0.wireOp",EDGE,"E0.right"),sQuery(id+"F0.wireOp",EDGE,"E0.left"),sQuery(id+"F0.wireOp",EDGE,"E3"),sQuery(id+"F0.wireOp",EDGE,"E5"),sQuery(id+"F0.wireOp",EDGE,"E6"),sQuery(id+"F0.wireOp",EDGE,"E7"),sQuery(id+"F0.wireOp",EDGE,"E8")])],"isStart":false}),makeQuery(id+"F3.opExtrude","CAP_FACE",FACE,{"disambiguationData":[OSD([sQuery(id+"F2.wireOp",EDGE,"E9"),sQuery(id+"F2.wireOp",EDGE,"E10"),sQuery(id+"F2.wireOp",EDGE,"E12"),sQuery(id+"F2.wireOp",EDGE,"E13"),sQuery(id+"F2.wireOp",EDGE,"E14"),sQuery(id+"F2.wireOp",EDGE,"E15"),sQuery(id+"F2.wireOp",EDGE,"E16")])],"isStart":false})]}),makeQuery(id+"F5.opExtrude","CAP_FACE",FACE,{"disambiguationData":[OSD([sQuery(id+"F4.wireOp",EDGE,"E19"),sQuery(id+"F4.wireOp",EDGE,"E20"),sQuery(id+"F4.wireOp",EDGE,"E21"),sQuery(id+"F4.wireOp",EDGE,"E22")])],"isStart":false})]});
            var sketch = newSketch(context, id + "F30", { "sketchPlane" : qUnion([Q0])});
            skCircle(sketch, "E95", {"center": v(22.25, 143) * mm, "radius": 3.16 * mm});
            skCircle(sketch, "E96", {"center": v(22.25, 143) * mm, "radius": 5.16 * mm});
            skCircle(sketch, "E97", {"center": v(22.25, 101) * mm, "radius": 3.16 * mm});
            skCircle(sketch, "E98", {"center": v(22.25, 101) * mm, "radius": 5.16 * mm});
            skSolve(sketch);
        }
        {
            var Q0;
            Q0 = qSketchRegion(id + "F30", true);
            var Q1;
            Q1=makeQuery(id+"FW9TydWOSUlmRxp_1.opExtrude","CAP_FACE",FACE,{"disambiguationData":[OSD([sQuery(id+"FSLd25ZuZ2697x5_1.wireOp",EDGE,"d7a39eb9-7608-4e6d-8ccc-f4c5e2293ca1"),sQuery(id+"FSLd25ZuZ2697x5_1.wireOp",EDGE,"b16bb200-7d67-433b-82d4-5dbab35da08e"),sQuery(id+"FSLd25ZuZ2697x5_1.wireOp",EDGE,"50e5177a-defd-4f2e-9e33-99e96e79239f"),sQuery(id+"FSLd25ZuZ2697x5_1.wireOp",EDGE,"a2fc24ef-a833-404e-a36b-78c50b66c55f"),sQuery(id+"FSLd25ZuZ2697x5_1.wireOp",EDGE,"647fb47b-25f9-4b46-bc29-06cc00dbe183"),sQuery(id+"FSLd25ZuZ2697x5_1.wireOp",EDGE,"3fc4816c-ed60-462a-8bf6-74485651d996"),sQuery(id+"FSLd25ZuZ2697x5_1.wireOp",EDGE,"f4c0511e-481e-4cf7-9e78-f592e706b1be"),sQuery(id+"FSLd25ZuZ2697x5_1.wireOp",EDGE,"961e0641-f87a-4cea-b1b3-242cdd40f9c0")])],"isStart":false});
            extrude(context, id + "F31", {"entities" : qUnion([Q0]), "operationType" : NewBodyOperationType.ADD, "endBoundEntityFace" : qUnion([Q1]), "depth" : 1.1 * mm});
        }
        {
            var Q0;
            Q0=makeQuery(id+"F5.boolean.opBoolean","MERGE",FACE,{"derivedFrom":[makeQuery(id+"F3.boolean.opBoolean","MERGE",FACE,{"derivedFrom":[makeQuery(id+"F1.opExtrude","CAP_FACE",FACE,{"disambiguationData":[OSD([sQuery(id+"F0.wireOp",EDGE,"E0.bottom"),sQuery(id+"F0.wireOp",EDGE,"E0.right"),sQuery(id+"F0.wireOp",EDGE,"E0.left"),sQuery(id+"F0.wireOp",EDGE,"E3"),sQuery(id+"F0.wireOp",EDGE,"E5"),sQuery(id+"F0.wireOp",EDGE,"E6"),sQuery(id+"F0.wireOp",EDGE,"E7"),sQuery(id+"F0.wireOp",EDGE,"E8")])],"isStart":false}),makeQuery(id+"F3.opExtrude","CAP_FACE",FACE,{"disambiguationData":[OSD([sQuery(id+"F2.wireOp",EDGE,"E9"),sQuery(id+"F2.wireOp",EDGE,"E10"),sQuery(id+"F2.wireOp",EDGE,"E12"),sQuery(id+"F2.wireOp",EDGE,"E13"),sQuery(id+"F2.wireOp",EDGE,"E14"),sQuery(id+"F2.wireOp",EDGE,"E15"),sQuery(id+"F2.wireOp",EDGE,"E16")])],"isStart":false})]}),makeQuery(id+"F5.opExtrude","CAP_FACE",FACE,{"disambiguationData":[OSD([sQuery(id+"F4.wireOp",EDGE,"E19"),sQuery(id+"F4.wireOp",EDGE,"E20"),sQuery(id+"F4.wireOp",EDGE,"E21"),sQuery(id+"F4.wireOp",EDGE,"E22")])],"isStart":false})]});
            var sketch = newSketch(context, id + "F32", { "sketchPlane" : qUnion([Q0])});
            skLineSegment(sketch, "E99.bottom", {"start": v(9, 207) * mm, "end": v(35.5, 207) * mm});
            skLineSegment(sketch, "E99.left", {"start": v(9, 207) * mm, "end": v(9, 167) * mm});
            skLineSegment(sketch, "E99.right", {"start": v(35.5, 207) * mm, "end": v(35.5, 167) * mm});
            skLineSegment(sketch, "E100.bottom", {"start": v(22.7, 203.2) * mm, "end": v(31.7, 203.2) * mm});
            skLineSegment(sketch, "E100.top", {"start": v(22.7, 193.7) * mm, "end": v(31.7, 193.7) * mm});
            skLineSegment(sketch, "E100.left", {"start": v(22.7, 203.2) * mm, "end": v(22.7, 193.7) * mm});
            skLineSegment(sketch, "E100.right", {"start": v(31.7, 203.2) * mm, "end": v(31.7, 193.7) * mm});
            skLineSegment(sketch, "E101", {"start": v(9, 167) * mm, "end": v(35.5, 167) * mm});
            skSolve(sketch);
        }
        {
            var Q0;
            Q0 = qSketchRegion(id + "F32", true);
            extrude(context, id + "F33", {"entities" : qUnion([Q0]), "operationType" : NewBodyOperationType.ADD, "depth" : 1 * mm});
        }
        {
            var Q0;
            Q0=makeQuery(id+"F33.opExtrude","CAP_FACE",FACE,{"disambiguationData":[OSD([sQuery(id+"F32.wireOp",EDGE,"E99.bottom"),sQuery(id+"F32.wireOp",EDGE,"E99.top"),sQuery(id+"F32.wireOp",EDGE,"E99.left"),sQuery(id+"F32.wireOp",EDGE,"E99.right"),sQuery(id+"F32.wireOp",EDGE,"E100.bottom"),sQuery(id+"F32.wireOp",EDGE,"E100.top"),sQuery(id+"F32.wireOp",EDGE,"E100.left"),sQuery(id+"F32.wireOp",EDGE,"E100.right")])],"isStart":false});
            var sketch = newSketch(context, id + "F34", { "sketchPlane" : qUnion([Q0])});
            skLineSegment(sketch, "E102.bottom", {"start": v(25.2, 203.2) * mm, "end": v(29.2, 203.2) * mm, "construction": true});
            skLineSegment(sketch, "E102.top", {"start": v(25.2, 204.4) * mm, "end": v(29.2, 204.4) * mm, "construction": true});
            skLineSegment(sketch, "E102.left", {"start": v(25.2, 203.2) * mm, "end": v(25.2, 204.4) * mm, "construction": true});
            skLineSegment(sketch, "E102.right", {"start": v(29.2, 203.2) * mm, "end": v(29.2, 204.4) * mm, "construction": true});
            skLineSegment(sketch, "E103", {"start": v(25.2, 204.4) * mm, "end": v(29.2, 204.4) * mm});
            skPoint(sketch, "E104", {"position": v(27.2, 203.2) * mm});
            skLineSegment(sketch, "E105.1.0", {"start": v(27.24, 193.98) * mm, "end": v(27.24, 203.5) * mm, "construction": true});
            skPoint(sketch, "E105.2.2", {"position": v(27.24, 193.97) * mm});
            skLineSegment(sketch, "E105.3.0", {"start": v(27.24, 203.5) * mm, "end": v(27.24, 193.98) * mm, "construction": true});
            skPoint(sketch, "E105.center", {"position": v(27.2, 198.44) * mm});
            skLineSegment(sketch, "E106.1.0", {"start": v(22.44, 196.44) * mm, "end": v(22.44, 200.44) * mm, "construction": true});
            skLineSegment(sketch, "E106.1.1", {"start": v(22.44, 200.44) * mm, "end": v(21.24, 200.44) * mm, "construction": true});
            skLineSegment(sketch, "E106.1.2", {"start": v(22.44, 196.44) * mm, "end": v(21.24, 196.44) * mm, "construction": true});
            skPoint(sketch, "E106.1.3", {"position": v(22.44, 198.44) * mm});
            skLineSegment(sketch, "E106.1.4", {"start": v(21.24, 196.44) * mm, "end": v(21.24, 200.44) * mm});
            skLineSegment(sketch, "E106.1.5", {"start": v(22.44, 196.44) * mm, "end": v(22.44, 200.44) * mm, "construction": true});
            skLineSegment(sketch, "E106.1.6", {"start": v(21.24, 196.44) * mm, "end": v(21.24, 200.44) * mm, "construction": true});
            skLineSegment(sketch, "E106.2.0", {"start": v(29.2, 193.68) * mm, "end": v(25.2, 193.68) * mm, "construction": true});
            skLineSegment(sketch, "E106.2.1", {"start": v(25.2, 193.68) * mm, "end": v(25.2, 192.48) * mm, "construction": true});
            skLineSegment(sketch, "E106.2.2", {"start": v(29.2, 193.68) * mm, "end": v(29.2, 192.48) * mm, "construction": true});
            skPoint(sketch, "E106.2.3", {"position": v(27.2, 193.68) * mm});
            skLineSegment(sketch, "E106.2.4", {"start": v(29.2, 192.48) * mm, "end": v(25.2, 192.48) * mm});
            skLineSegment(sketch, "E106.2.5", {"start": v(29.2, 193.68) * mm, "end": v(25.2, 193.68) * mm, "construction": true});
            skLineSegment(sketch, "E106.2.6", {"start": v(29.2, 192.48) * mm, "end": v(25.2, 192.48) * mm, "construction": true});
            skLineSegment(sketch, "E107.1.3.0", {"start": v(31.96, 200.44) * mm, "end": v(31.96, 196.44) * mm, "construction": true});
            skLineSegment(sketch, "E107.3.3.0", {"start": v(31.96, 196.44) * mm, "end": v(33.16, 196.44) * mm, "construction": true});
            skLineSegment(sketch, "E107.6.3.0", {"start": v(31.96, 200.44) * mm, "end": v(33.16, 200.44) * mm, "construction": true});
            skPoint(sketch, "E107.9.3.0", {"position": v(31.96, 198.44) * mm});
            skLineSegment(sketch, "E107.10.3.0", {"start": v(33.16, 200.44) * mm, "end": v(33.16, 196.44) * mm});
            skLineSegment(sketch, "E107.13.3.0", {"start": v(31.96, 200.44) * mm, "end": v(31.96, 196.44) * mm, "construction": true});
            skLineSegment(sketch, "E107.16.3.0", {"start": v(33.16, 200.44) * mm, "end": v(33.16, 196.44) * mm, "construction": true});
            skArc(sketch, "E108", {"start": v(25.2, 204.4) * mm, "mid": v(22.4, 203.24) * mm, "end": v(21.24, 200.44) * mm});
            skArc(sketch, "E109", {"start": v(21.24, 196.44) * mm, "mid": v(22.4, 193.64) * mm, "end": v(25.2, 192.48) * mm});
            skArc(sketch, "E110", {"start": v(33.16, 200.44) * mm, "mid": v(32, 203.24) * mm, "end": v(29.2, 204.4) * mm});
            skArc(sketch, "E111", {"start": v(29.2, 192.48) * mm, "mid": v(32, 193.64) * mm, "end": v(33.16, 196.44) * mm});
            skLineSegment(sketch, "E112.0", {"start": v(25.2, 206) * mm, "end": v(29.2, 206) * mm});
            skArc(sketch, "E112.1", {"start": v(34.76, 200.44) * mm, "mid": v(33.13, 204.37) * mm, "end": v(29.2, 206) * mm});
            skArc(sketch, "E112.2", {"start": v(25.2, 206) * mm, "mid": v(21.27, 204.37) * mm, "end": v(19.64, 200.44) * mm});
            skLineSegment(sketch, "E112.3", {"start": v(34.76, 200.44) * mm, "end": v(34.76, 196.44) * mm});
            skLineSegment(sketch, "E112.4", {"start": v(19.64, 196.44) * mm, "end": v(19.64, 200.44) * mm});
            skArc(sketch, "E112.5", {"start": v(19.64, 196.44) * mm, "mid": v(21.27, 192.5) * mm, "end": v(25.2, 190.88) * mm});
            skLineSegment(sketch, "E112.6", {"start": v(29.2, 190.88) * mm, "end": v(25.2, 190.88) * mm});
            skArc(sketch, "E112.7", {"start": v(29.2, 190.88) * mm, "mid": v(33.13, 192.5) * mm, "end": v(34.76, 196.44) * mm});
            skSolve(sketch);
        }
        {
            var Q0;
            Q0 = qSketchRegion(id + "F34", true);
            var Q1;
            Q1=makeQuery(id+"F23.opExtrude","CAP_FACE",FACE,{"disambiguationData":[OSD([sQuery(id+"F22.wireOp",EDGE,"E84.bottom"),sQuery(id+"F22.wireOp",EDGE,"E84.top"),sQuery(id+"F22.wireOp",EDGE,"E84.left"),sQuery(id+"F22.wireOp",EDGE,"E84.right")])],"isStart":false});
            extrude(context, id + "F35", {"entities" : qUnion([Q0]), "operationType" : NewBodyOperationType.REMOVE, "endBound" : BoundingType.UP_TO_SURFACE, "oppositeDirection" : true, "endBoundEntityFace" : qUnion([Q1]), "depth" : 1 * mm});
        }
        {
            var Q0;
            {var subQ0=sQuery(id+"F32.wireOp",EDGE,"E99.bottom");var subQ1=sQuery(id+"F32.wireOp",EDGE,"E99.left");var subQ2=sQuery(id+"F32.wireOp",EDGE,"E99.right");var subQ3=sQuery(id+"F32.wireOp",EDGE,"c7c3d2cf-ceb9-4799-9851-c5ddec76fa12");var subQ4=sQuery(id+"F32.wireOp",EDGE,"664628c1-fd01-417f-add4-858e87ab8833");Q0=makeQuery(id+"F35.boolean.opBoolean","SPLIT",FACE,{"disambiguationData":[TD([makeQuery(id+"F3.opExtrude","SWEPT_FACE",FACE,{"disambiguationData":[OSD([sQuery(id+"F2.wireOp",EDGE,"E15")])]})])],"derivedFrom":makeQuery(id+"F33.opExtrude","CAP_FACE",FACE,{"disambiguationData":[OSD([subQ0,subQ1,subQ2,sQuery(id+"F32.wireOp",EDGE,"E100.bottom"),sQuery(id+"F32.wireOp",EDGE,"E100.top"),sQuery(id+"F32.wireOp",EDGE,"E100.left"),sQuery(id+"F32.wireOp",EDGE,"E100.right"),subQ3,subQ4])],"isStart":false})});}
            var sketch = newSketch(context, id + "F36", { "sketchPlane" : qUnion([Q0])});
            skLineSegment(sketch, "E113.bottom", {"start": v(17.14, 207) * mm, "end": v(35.5, 207) * mm});
            skLineSegment(sketch, "E113.top", {"start": v(25.14, 188.38) * mm, "end": v(35.5, 188.38) * mm});
            skLineSegment(sketch, "E113.left", {"start": v(17.14, 207) * mm, "end": v(17.14, 196.38) * mm});
            skLineSegment(sketch, "E113.right", {"start": v(35.5, 207) * mm, "end": v(35.5, 188.38) * mm});
            skPoint(sketch, "E114.visualSharp", {"position": v(17.14, 188.38) * mm});
            skArc(sketch, "E114.filletArc", {"start": v(17.14, 196.38) * mm, "mid": v(19.48, 190.72) * mm, "end": v(25.14, 188.38) * mm});
            skLineSegment(sketch, "E115", {"start": v(25.2, 204.4) * mm, "end": v(29.2, 204.4) * mm});
            skArc(sketch, "E116", {"start": v(33.16, 200.44) * mm, "mid": v(32, 203.24) * mm, "end": v(29.2, 204.4) * mm});
            skLineSegment(sketch, "E117", {"start": v(21.24, 200.44) * mm, "end": v(21.24, 196.44) * mm});
            skLineSegment(sketch, "E118", {"start": v(25.2, 192.48) * mm, "end": v(29.2, 192.48) * mm});
            skLineSegment(sketch, "E119", {"start": v(33.16, 196.44) * mm, "end": v(33.16, 200.44) * mm});
            skArc(sketch, "E120", {"start": v(29.2, 192.48) * mm, "mid": v(32, 193.64) * mm, "end": v(33.16, 196.44) * mm});
            skArc(sketch, "E121", {"start": v(21.24, 196.44) * mm, "mid": v(22.4, 193.64) * mm, "end": v(25.2, 192.48) * mm});
            skArc(sketch, "E122", {"start": v(25.2, 204.4) * mm, "mid": v(22.4, 203.24) * mm, "end": v(21.24, 200.44) * mm});
            skSolve(sketch);
        }
        {
            var Q0;
            Q0 = qSketchRegion(id + "F36", true);
            extrude(context, id + "F37", {"entities" : qUnion([Q0]), "operationType" : NewBodyOperationType.REMOVE, "oppositeDirection" : true, "depth" : 1 * mm});
        }
        {
            var Q0;
            Q0=makeQuery(id+"F33.opExtrude","CAP_EDGE",EDGE,{"disambiguationData":[OSD([sQuery(id+"F32.wireOp",EDGE,"E101")])],"isStart":false});
            fillet(context, id + "F38", {"entities" : qUnion([Q0]), "radius" : 15 * mm, "tangentPropagation" : true, "allowEdgeOverflow" : false});
        }
        {
            var Q0;
            {var subQ0=sQuery(id+"F32.wireOp",EDGE,"E100.bottom");var subQ1=sQuery(id+"F32.wireOp",EDGE,"E100.top");var subQ2=sQuery(id+"F32.wireOp",EDGE,"E100.left");var subQ3=sQuery(id+"F32.wireOp",EDGE,"E100.right");Q0=makeQuery(id+"F35.boolean.opBoolean","SPLIT",FACE,{"disambiguationData":[TD([makeQuery(id+"F11.boolean.opBoolean","COPY",FACE,{"derivedFrom":makeQuery(id+"F11.opExtrude","SWEPT_FACE",FACE,{"disambiguationData":[OSD([sQuery(id+"F10.wireOp",EDGE,"E43.bottom")])]})})])],"derivedFrom":makeQuery(id+"F33.opExtrude","CAP_FACE",FACE,{"disambiguationData":[OSD([sQuery(id+"F32.wireOp",EDGE,"E99.bottom"),sQuery(id+"F32.wireOp",EDGE,"E99.left"),sQuery(id+"F32.wireOp",EDGE,"E99.right"),subQ0,subQ1,subQ2,subQ3,sQuery(id+"F32.wireOp",EDGE,"E101")])],"isStart":false})});}
            var sketch = newSketch(context, id + "F39", { "sketchPlane" : qUnion([Q0])});
            skLineSegment(sketch, "E123.bottom", {"start": v(23.8, 202.1) * mm, "end": v(21.6, 202.1) * mm});
            skLineSegment(sketch, "E123.top", {"start": v(23.8, 204.3) * mm, "end": v(21.6, 204.3) * mm});
            skLineSegment(sketch, "E123.left", {"start": v(23.8, 202.1) * mm, "end": v(23.8, 204.3) * mm});
            skLineSegment(sketch, "E123.right", {"start": v(21.6, 202.1) * mm, "end": v(21.6, 204.3) * mm});
            skLineSegment(sketch, "E124", {"start": v(21.6, 203.2) * mm, "end": v(23.8, 203.2) * mm, "construction": true});
            skLineSegment(sketch, "E125", {"start": v(22.7, 204.3) * mm, "end": v(22.7, 202.1) * mm, "construction": true});
            skPoint(sketch, "E126.center", {"position": v(27.2, 198.44) * mm});
            skLineSegment(sketch, "E127.bottom", {"start": v(32.8, 202.1) * mm, "end": v(30.6, 202.1) * mm});
            skLineSegment(sketch, "E127.right", {"start": v(30.6, 202.1) * mm, "end": v(30.6, 204.3) * mm});
            skLineSegment(sketch, "E128", {"start": v(31.7, 204.3) * mm, "end": v(31.7, 202.1) * mm, "construction": true});
            skLineSegment(sketch, "E127.left", {"start": v(32.8, 202.1) * mm, "end": v(32.8, 204.3) * mm});
            skLineSegment(sketch, "E129", {"start": v(30.6, 203.2) * mm, "end": v(32.8, 203.2) * mm, "construction": true});
            skLineSegment(sketch, "E127.top", {"start": v(32.8, 204.3) * mm, "end": v(30.6, 204.3) * mm});
            skLineSegment(sketch, "E130.bottom", {"start": v(32.8, 192.6) * mm, "end": v(30.6, 192.6) * mm});
            skLineSegment(sketch, "E130.right", {"start": v(30.6, 192.6) * mm, "end": v(30.6, 194.8) * mm});
            skLineSegment(sketch, "E131", {"start": v(31.7, 194.8) * mm, "end": v(31.7, 192.6) * mm, "construction": true});
            skLineSegment(sketch, "E130.left", {"start": v(32.8, 192.6) * mm, "end": v(32.8, 194.8) * mm});
            skLineSegment(sketch, "E132", {"start": v(30.6, 193.7) * mm, "end": v(32.8, 193.7) * mm, "construction": true});
            skLineSegment(sketch, "E130.top", {"start": v(32.8, 194.8) * mm, "end": v(30.6, 194.8) * mm});
            skLineSegment(sketch, "E133.bottom", {"start": v(23.8, 192.6) * mm, "end": v(21.6, 192.6) * mm});
            skLineSegment(sketch, "E133.right", {"start": v(21.6, 192.6) * mm, "end": v(21.6, 194.8) * mm});
            skLineSegment(sketch, "E134", {"start": v(22.7, 194.8) * mm, "end": v(22.7, 192.6) * mm, "construction": true});
            skLineSegment(sketch, "E133.left", {"start": v(23.8, 192.6) * mm, "end": v(23.8, 194.8) * mm});
            skLineSegment(sketch, "E135", {"start": v(21.6, 193.7) * mm, "end": v(23.8, 193.7) * mm, "construction": true});
            skLineSegment(sketch, "E133.top", {"start": v(23.8, 194.8) * mm, "end": v(21.6, 194.8) * mm});
            skSolve(sketch);
        }
        {
            var Q0;
            Q0 = qSketchRegion(id + "F39", true);
            var Q1;
            Q1=makeQuery(id+"F37.boolean.opBoolean","COPY",FACE,{"derivedFrom":makeQuery(id+"F37.opExtrude","CAP_FACE",FACE,{"disambiguationData":[OSD([sQuery(id+"F36.wireOp",EDGE,"E113.bottom"),sQuery(id+"F36.wireOp",EDGE,"E113.top"),sQuery(id+"F36.wireOp",EDGE,"E113.left"),sQuery(id+"F36.wireOp",EDGE,"E113.right"),sQuery(id+"F36.wireOp",EDGE,"E114.filletArc"),sQuery(id+"F36.wireOp",EDGE,"E115"),sQuery(id+"F36.wireOp",EDGE,"E116"),sQuery(id+"F36.wireOp",EDGE,"E117"),sQuery(id+"F36.wireOp",EDGE,"E118"),sQuery(id+"F36.wireOp",EDGE,"E119"),sQuery(id+"F36.wireOp",EDGE,"E120"),sQuery(id+"F36.wireOp",EDGE,"E121"),sQuery(id+"F36.wireOp",EDGE,"E122")])],"isStart":false})});
            extrude(context, id + "F40", {"entities" : qUnion([Q0]), "operationType" : NewBodyOperationType.REMOVE, "endBound" : BoundingType.UP_TO_SURFACE, "oppositeDirection" : true, "endBoundEntityFace" : qUnion([Q1]), "depth" : 25 * mm});
        }
    });
